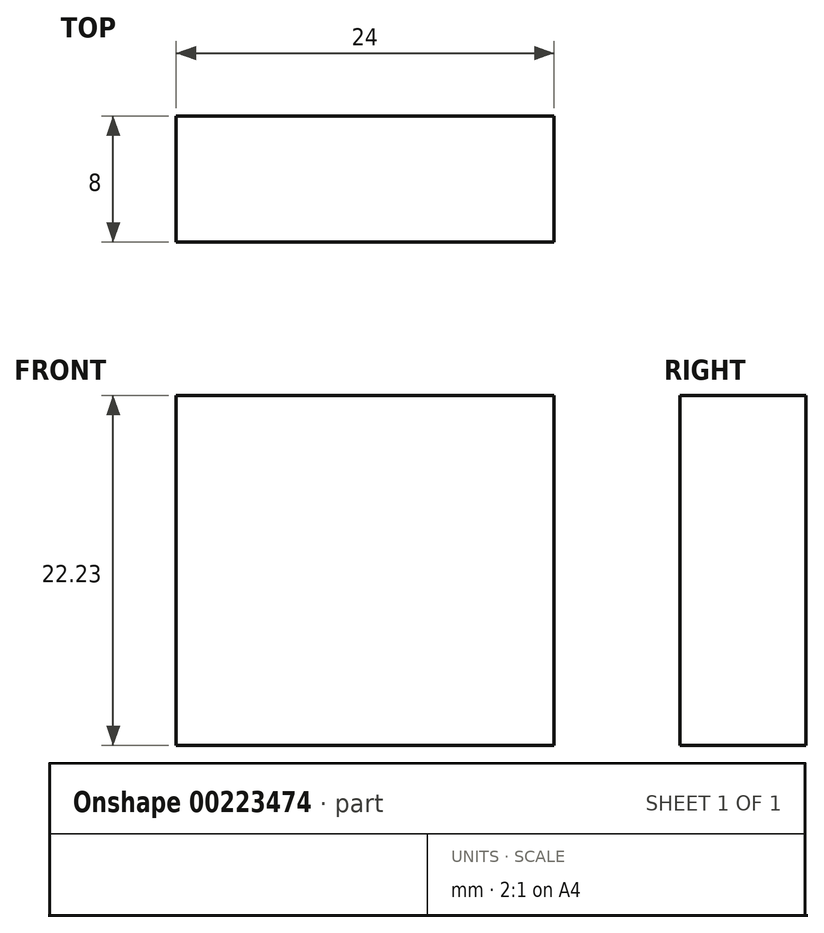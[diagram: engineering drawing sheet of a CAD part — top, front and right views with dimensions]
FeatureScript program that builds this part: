
annotation { "Feature Type Name" : "Feature", "Feature Type Description" : "" }
export const myFeature = defineFeature(function(context is Context, id is Id, definition is map)
    precondition{}
    {
        {
            var Q0;
            Q0=qCreatedBy(makeId("Front.planeOp"),FACE);
            var sketch = newSketch(context, id + "F0", { "sketchPlane" : qUnion([Q0])});
            skLineSegment(sketch, "E0", {"start": v(-67.66, -74.97) * mm, "end": v(-43.66, -74.97) * mm});
            skLineSegment(sketch, "E1", {"start": v(-43.66, -74.97) * mm, "end": v(-43.66, -52.74) * mm});
            skLineSegment(sketch, "E2", {"start": v(-43.66, -52.74) * mm, "end": v(-67.66, -52.74) * mm});
            skLineSegment(sketch, "E3", {"start": v(-67.66, -52.74) * mm, "end": v(-67.66, -74.97) * mm});
            skSolve(sketch);
        }
        {
            var Q0;
            Q0=makeQuery(id+"F0.imprint","IMPRINT",FACE,{"disambiguationData":[TD([[makeQuery(id+"F0.imprint","IMPRINT",EDGE,{"derivedFrom":sQuery(id+"F0.wireOp",EDGE,"E0")}),1.0]])]});
            extrude(context, id + "F1", {"entities" : qUnion([Q0]), "oppositeDirection" : true, "depth" : 8 * mm});
        }
    });
